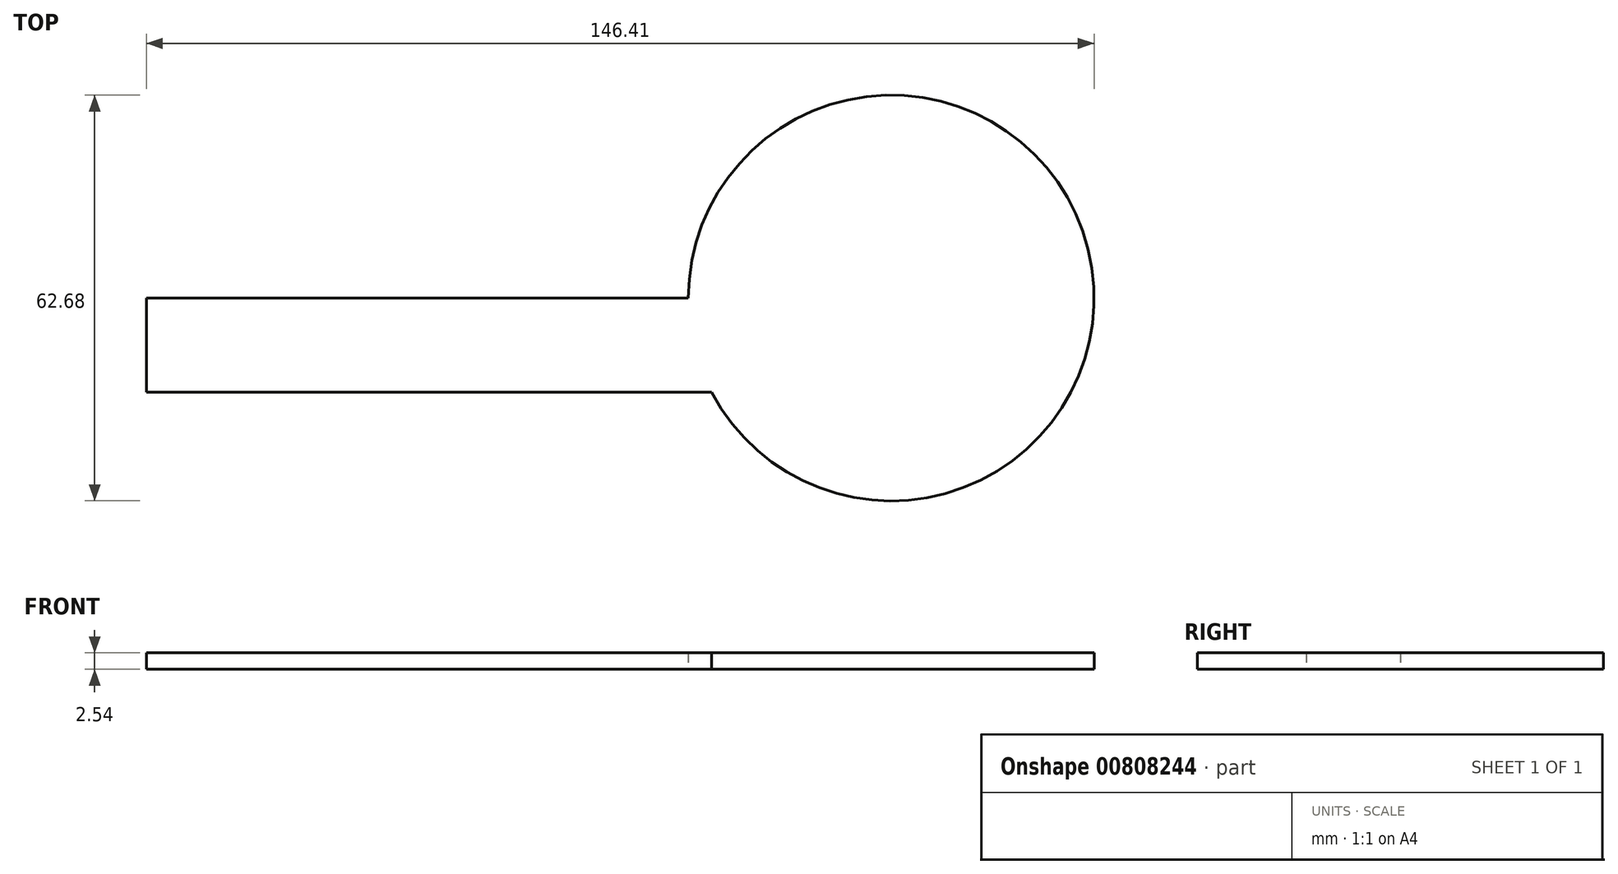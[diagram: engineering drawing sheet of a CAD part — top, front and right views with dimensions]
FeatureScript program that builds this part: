
annotation { "Feature Type Name" : "Feature", "Feature Type Description" : "" }
export const myFeature = defineFeature(function(context is Context, id is Id, definition is map)
    precondition{}
    {
        {
            var Q0;
            Q0=qCreatedBy(makeId("Top.planeOp"),FACE);
            var sketch = newSketch(context, id + "F0", { "sketchPlane" : qUnion([Q0])});
            skCircle(sketch, "E0", {"center": v(0, 0) * mm, "radius": 31.34 * mm});
            skLineSegment(sketch, "E1.bottom", {"start": v(0, 0) * mm, "end": v(-115.07, 0) * mm});
            skLineSegment(sketch, "E1.top", {"start": v(0, -14.57) * mm, "end": v(-115.07, -14.57) * mm});
            skLineSegment(sketch, "E1.left", {"start": v(0, 0) * mm, "end": v(0, -14.57) * mm});
            skLineSegment(sketch, "E1.right", {"start": v(-115.07, 0) * mm, "end": v(-115.07, -14.57) * mm});
            skSolve(sketch);
        }
        {
            var Q0;
            {var subQ5=sQuery(id+"F0.wireOp",EDGE,"E1.right");Q0=makeQuery(id+"F0.imprint","IMPRINT",FACE,{"disambiguationData":[TD([[makeQuery(id+"F0.imprint","IMPRINT",EDGE,{"derivedFrom":subQ5}),1.0]])]});}
            extrude(context, id + "F1", {"entities" : qUnion([Q0]), "depth" : 2.54 * mm, "offsetDistance" : 25.4 * mm});
        }
        {
            var Q0;
            {var subQ5=sQuery(id+"F0.wireOp",EDGE,"E1.left");Q0=makeQuery(id+"F0.imprint","IMPRINT",FACE,{"disambiguationData":[TD([[makeQuery(id+"F0.imprint","IMPRINT",EDGE,{"derivedFrom":subQ5}),-1.0]])]});}
            var Q1;
            {var subQ5=sQuery(id+"F0.wireOp",EDGE,"E1.left");Q1=makeQuery(id+"F0.imprint","IMPRINT",FACE,{"disambiguationData":[TD([[makeQuery(id+"F0.imprint","IMPRINT",EDGE,{"derivedFrom":subQ5}),1.0]])]});}
            extrude(context, id + "F2", {"entities" : qUnion([Q0, Q1]), "operationType" : NewBodyOperationType.ADD, "depth" : 2.54 * mm, "offsetDistance" : 25.4 * mm});
        }
    });
